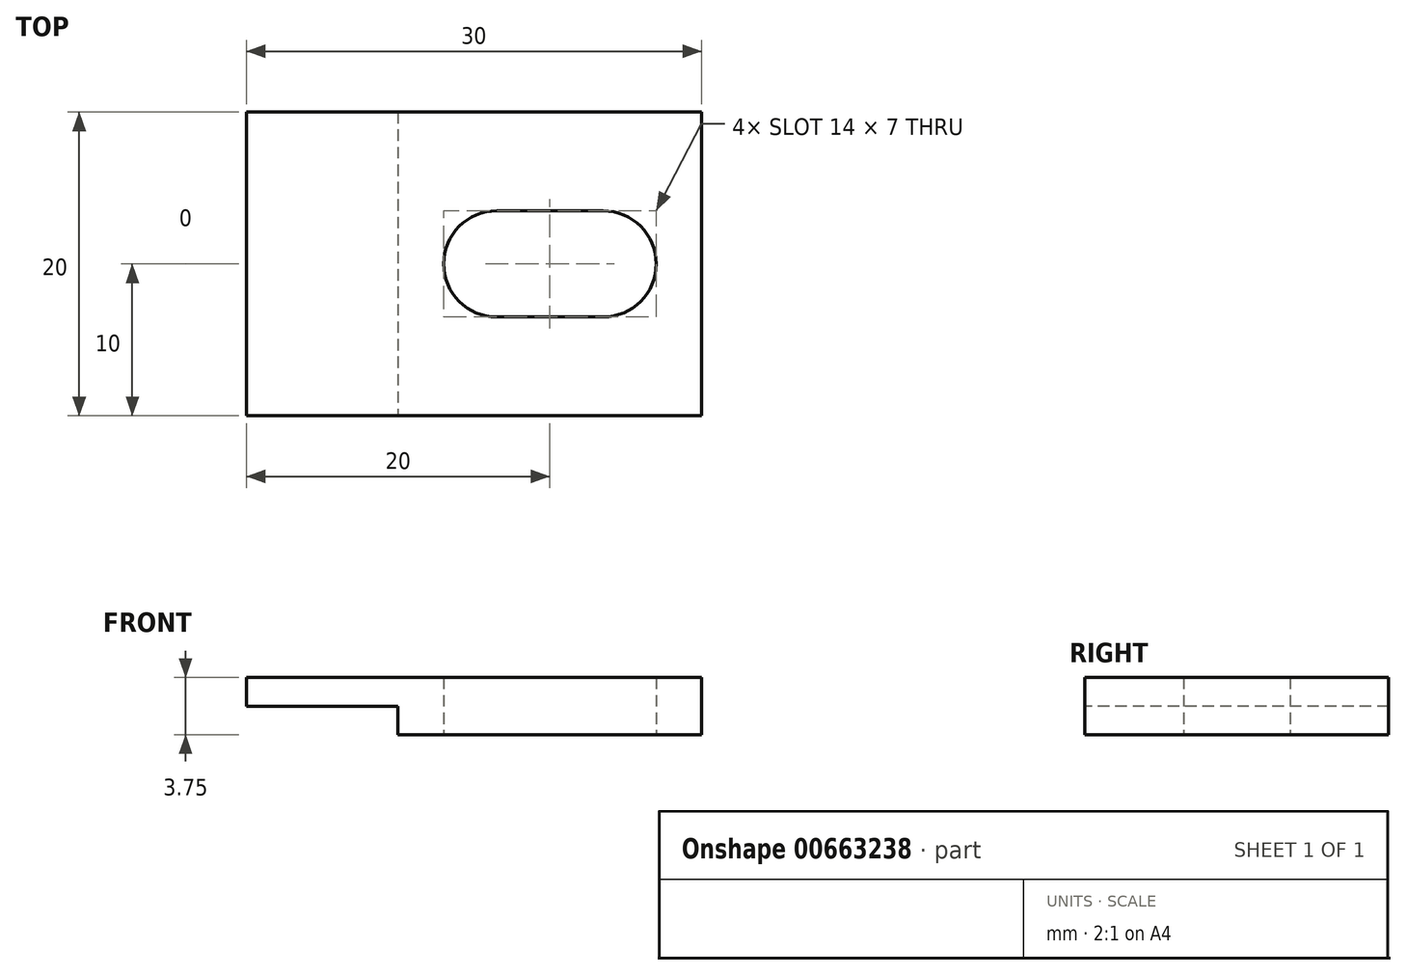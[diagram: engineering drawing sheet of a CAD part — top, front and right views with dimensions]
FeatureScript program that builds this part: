
annotation { "Feature Type Name" : "Feature", "Feature Type Description" : "" }
export const myFeature = defineFeature(function(context is Context, id is Id, definition is map)
    precondition{}
    {
        {
            var Q0;
            Q0=qCreatedBy(makeId("Top.planeOp"),FACE);
            var sketch = newSketch(context, id + "F0", { "sketchPlane" : qUnion([Q0])});
            skLineSegment(sketch, "E0.bottom", {"start": v(15, -10) * mm, "end": v(-15, -10) * mm});
            skLineSegment(sketch, "E0.top", {"start": v(15, 10) * mm, "end": v(-15, 10) * mm});
            skLineSegment(sketch, "E0.left", {"start": v(15, -10) * mm, "end": v(15, 10) * mm});
            skLineSegment(sketch, "E0.right", {"start": v(-15, -10) * mm, "end": v(-15, 10) * mm});
            skPoint(sketch, "E0.middle", {"position": v(0, 0) * mm});
            skSolve(sketch);
        }
        {
            var Q0;
            Q0=makeQuery(id+"F0.imprint","IMPRINT",FACE,{"disambiguationData":[TD([[makeQuery(id+"F0.imprint","IMPRINT",EDGE,{"derivedFrom":sQuery(id+"F0.wireOp",EDGE,"E0.bottom")}),-1.0]])]});
            extrude(context, id + "F1", {"entities" : qUnion([Q0]), "depth" : 3.75 * mm, "offsetDistance" : 25 * mm});
        }
        {
            var Q0;
            Q0=makeQuery(id+"F1.opExtrude","SWEPT_FACE",FACE,{"disambiguationData":[OSD([sQuery(id+"F0.wireOp",EDGE,"E0.bottom")])]});
            var sketch = newSketch(context, id + "F2", { "sketchPlane" : qUnion([Q0])});
            skLineSegment(sketch, "E1.bottom", {"start": v(-15, 0) * mm, "end": v(-5, 0) * mm});
            skLineSegment(sketch, "E1.top", {"start": v(-15, 1.88) * mm, "end": v(-5, 1.88) * mm});
            skLineSegment(sketch, "E1.left", {"start": v(-15, 0) * mm, "end": v(-15, 1.88) * mm});
            skLineSegment(sketch, "E1.right", {"start": v(-5, 0) * mm, "end": v(-5, 1.88) * mm});
            skSolve(sketch);
        }
        {
            var Q0;
            Q0=makeQuery(id+"F2.imprint","IMPRINT",FACE,{"disambiguationData":[TD([[makeQuery(id+"F2.imprint","IMPRINT",EDGE,{"derivedFrom":sQuery(id+"F2.wireOp",EDGE,"E1.bottom")}),-1.0]])]});
            extrude(context, id + "F3", {"entities" : qUnion([Q0]), "operationType" : NewBodyOperationType.REMOVE, "oppositeDirection" : true, "depth" : 24.3 * mm, "offsetDistance" : 25 * mm});
        }
        {
            var Q0;
            Q0=makeQuery(id+"F1.opExtrude","CAP_FACE",FACE,{"disambiguationData":[OSD([sQuery(id+"F0.wireOp",EDGE,"E0.bottom"),sQuery(id+"F0.wireOp",EDGE,"E0.top"),sQuery(id+"F0.wireOp",EDGE,"E0.left"),sQuery(id+"F0.wireOp",EDGE,"E0.right")])],"isStart":true});
            var sketch = newSketch(context, id + "F4", { "sketchPlane" : qUnion([Q0])});
            skCircle(sketch, "E2", {"center": v(1.5, 0) * mm, "radius": 3.5 * mm});
            skCircle(sketch, "E3", {"center": v(8.5, 0) * mm, "radius": 3.5 * mm});
            skLineSegment(sketch, "E4", {"start": v(1.5, -3.5) * mm, "end": v(8.5, -3.5) * mm});
            skLineSegment(sketch, "E5", {"start": v(1.5, 3.5) * mm, "end": v(8.5, 3.5) * mm});
            skSolve(sketch);
        }
        {
            var Q0;
            {var subQ0=sQuery(id+"F4.wireOp",EDGE,"E2");var subQ1=makeQuery(id+"F4.imprint","INTERSECT",VERTEX,{"derivedFrom":[subQ0,sQuery(id+"F4.wireOp",EDGE,"E5")]});Q0=makeQuery(id+"F4.imprint","IMPRINT",FACE,{"disambiguationData":[TD([[makeQuery(id+"F4.imprint","IMPRINT",EDGE,{"disambiguationData":[TD([[subQ1,1.0]])],"derivedFrom":subQ0}),1.0]])]});}
            var Q1;
            {var subQ0=sQuery(id+"F4.wireOp",EDGE,"E5");Q1=makeQuery(id+"F4.imprint","IMPRINT",FACE,{"disambiguationData":[TD([[makeQuery(id+"F4.imprint","IMPRINT",EDGE,{"derivedFrom":subQ0}),-1.0]])]});}
            var Q2;
            {var subQ0=sQuery(id+"F4.wireOp",EDGE,"E4");Q2=makeQuery(id+"F4.imprint","IMPRINT",FACE,{"disambiguationData":[TD([[makeQuery(id+"F4.imprint","IMPRINT",EDGE,{"derivedFrom":subQ0}),1.0]])]});}
            var Q3;
            {var subQ0=sQuery(id+"F4.wireOp",EDGE,"E3");var subQ1=makeQuery(id+"F4.imprint","INTERSECT",VERTEX,{"derivedFrom":[subQ0,sQuery(id+"F4.wireOp",EDGE,"E5")]});Q3=makeQuery(id+"F4.imprint","IMPRINT",FACE,{"disambiguationData":[TD([[makeQuery(id+"F4.imprint","IMPRINT",EDGE,{"disambiguationData":[TD([[subQ1,-1.0]])],"derivedFrom":subQ0}),1.0]])]});}
            extrude(context, id + "F5", {"entities" : qUnion([Q0, Q1, Q2, Q3]), "operationType" : NewBodyOperationType.REMOVE, "oppositeDirection" : true, "depth" : 16.12 * mm, "offsetDistance" : 25 * mm});
        }
    });
